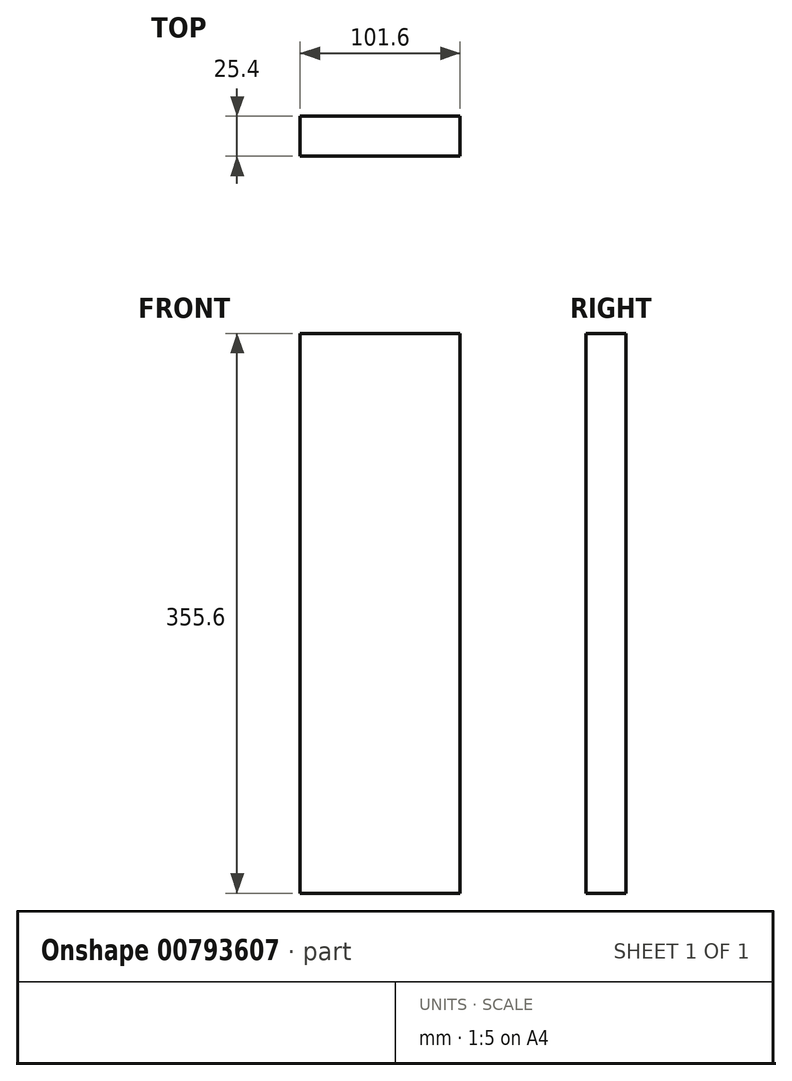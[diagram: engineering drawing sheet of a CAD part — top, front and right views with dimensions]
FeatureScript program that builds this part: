
annotation { "Feature Type Name" : "Feature", "Feature Type Description" : "" }
export const myFeature = defineFeature(function(context is Context, id is Id, definition is map)
    precondition{}
    {
        {
            var Q0;
            Q0=qCreatedBy(makeId("Front.planeOp"),FACE);
            var sketch = newSketch(context, id + "F0", { "sketchPlane" : qUnion([Q0])});
            skLineSegment(sketch, "E0.bottom", {"start": v(0, 0) * mm, "end": v(-101.6, 0) * mm});
            skLineSegment(sketch, "E0.top", {"start": v(0, 355.6) * mm, "end": v(-101.6, 355.6) * mm});
            skLineSegment(sketch, "E0.left", {"start": v(0, 0) * mm, "end": v(0, 355.6) * mm});
            skLineSegment(sketch, "E0.right", {"start": v(-101.6, 0) * mm, "end": v(-101.6, 355.6) * mm});
            skSolve(sketch);
        }
        {
            var Q0;
            Q0=makeQuery(id+"F0.imprint","IMPRINT",FACE,{"disambiguationData":[TD([[makeQuery(id+"F0.imprint","IMPRINT",EDGE,{"derivedFrom":sQuery(id+"F0.wireOp",EDGE,"E0.bottom")}),-1.0]])]});
            extrude(context, id + "F1", {"entities" : qUnion([Q0]), "oppositeDirection" : true, "depth" : 25.4 * mm, "offsetDistance" : 25 * mm});
        }
    });
